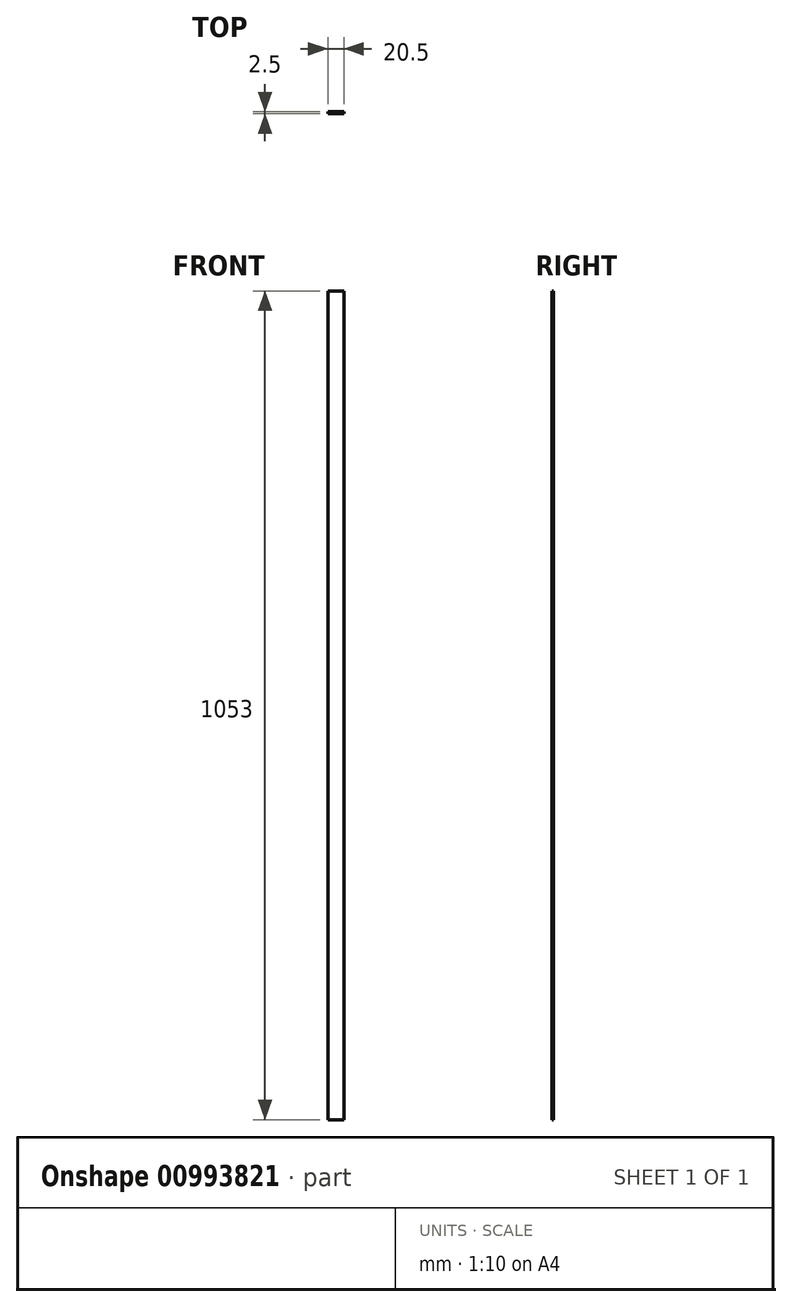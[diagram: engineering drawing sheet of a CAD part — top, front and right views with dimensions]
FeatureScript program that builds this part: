
annotation { "Feature Type Name" : "Feature", "Feature Type Description" : "" }
export const myFeature = defineFeature(function(context is Context, id is Id, definition is map)
    precondition{}
    {
        {
            var Q0;
            Q0=qCreatedBy(makeId("Top.planeOp"),FACE);
            var sketch = newSketch(context, id + "F0", { "sketchPlane" : qUnion([Q0])});
            skLineSegment(sketch, "E0.bottom", {"start": v(10.25, 1.25) * mm, "end": v(-10.25, 1.25) * mm});
            skLineSegment(sketch, "E0.top", {"start": v(10.25, -1.25) * mm, "end": v(-10.25, -1.25) * mm});
            skLineSegment(sketch, "E0.left", {"start": v(10.25, 1.25) * mm, "end": v(10.25, -1.25) * mm});
            skLineSegment(sketch, "E0.right", {"start": v(-10.25, 1.25) * mm, "end": v(-10.25, -1.25) * mm});
            skPoint(sketch, "E0.middle", {"position": v(0, 0) * mm});
            skSolve(sketch);
        }
        {
            var Q0;
            Q0=makeQuery(id+"F0.imprint","IMPRINT",FACE,{"disambiguationData":[TD([[makeQuery(id+"F0.imprint","IMPRINT",EDGE,{"derivedFrom":sQuery(id+"F0.wireOp",EDGE,"E0.bottom")}),1.0]])]});
            extrude(context, id + "F1", {"entities" : qUnion([Q0]), "depth" : 1053 * mm, "offsetDistance" : 25 * mm, "symmetric" : true});
        }
    });
